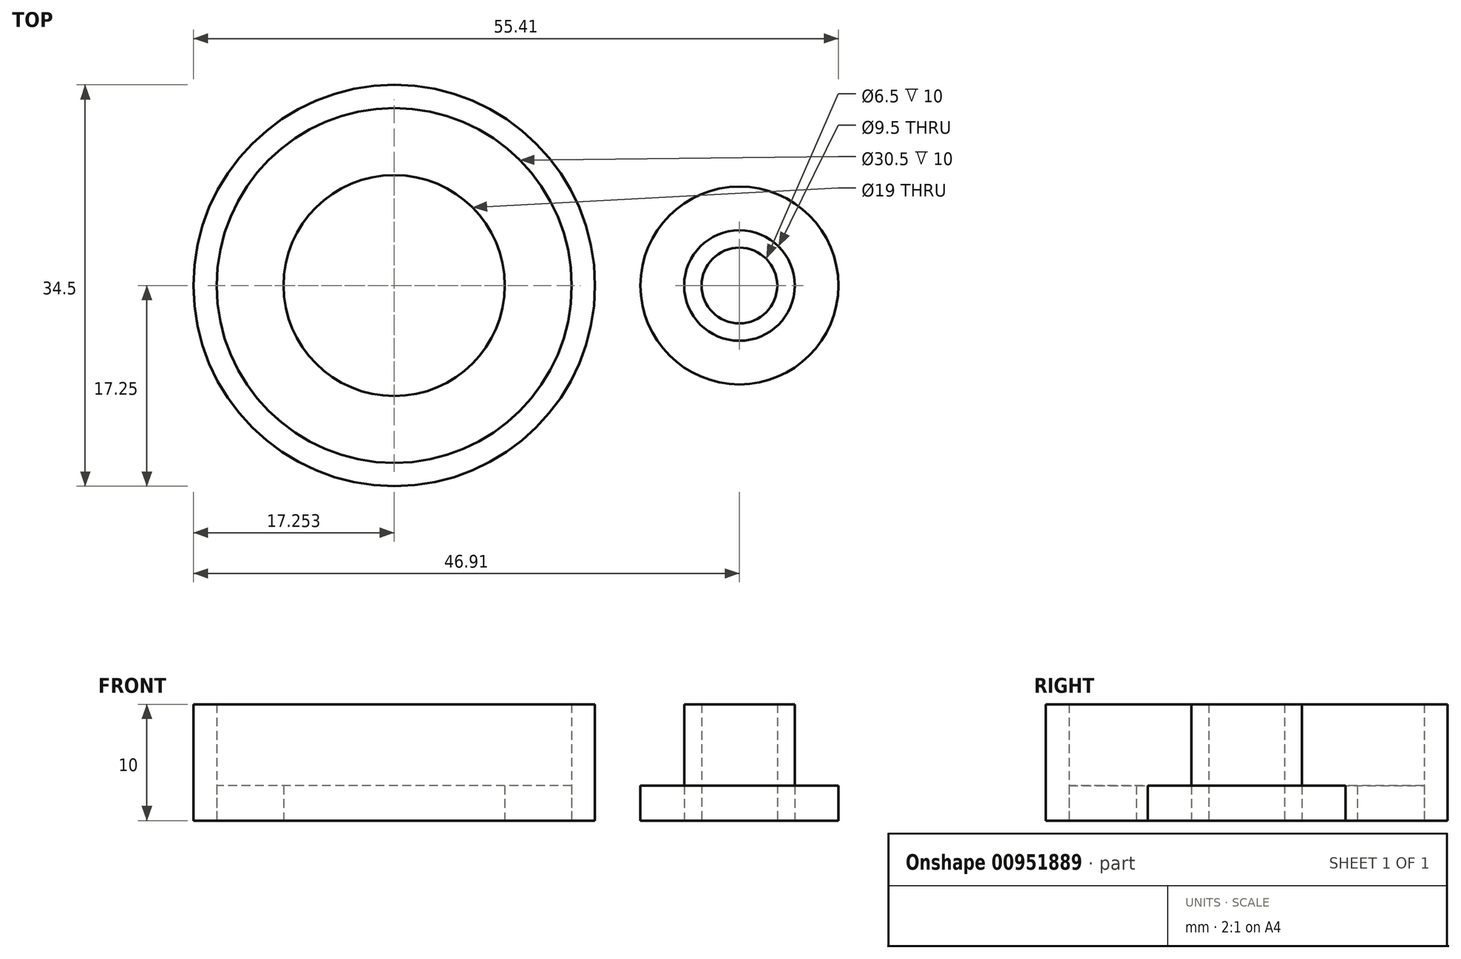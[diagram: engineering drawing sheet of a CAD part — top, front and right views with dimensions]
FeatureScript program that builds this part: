
annotation { "Feature Type Name" : "Feature", "Feature Type Description" : "" }
export const myFeature = defineFeature(function(context is Context, id is Id, definition is map)
    precondition{}
    {
        {
            var Q0;
            Q0=qCreatedBy(makeId("Top.planeOp"),FACE);
            var sketch = newSketch(context, id + "F0", { "sketchPlane" : qUnion([Q0])});
            skCircle(sketch, "E0", {"center": v(-39.15, 0) * mm, "radius": 15.25 * mm});
            skCircle(sketch, "E1", {"center": v(-39.15, 0) * mm, "radius": 17.25 * mm});
            skCircle(sketch, "E2", {"center": v(-9.5, 0) * mm, "radius": 4.75 * mm});
            skCircle(sketch, "E3", {"center": v(-9.5, 0) * mm, "radius": 8.5 * mm});
            skCircle(sketch, "E4", {"center": v(-9.5, 0) * mm, "radius": 3.25 * mm});
            skCircle(sketch, "E5", {"center": v(-39.15, 0) * mm, "radius": 9.5 * mm});
            skSolve(sketch);
        }
        {
            var Q0;
            Q0=makeQuery(id+"F0.imprint","IMPRINT",FACE,{"disambiguationData":[TD([[makeQuery(id+"F0.imprint","IMPRINT",EDGE,{"derivedFrom":sQuery(id+"F0.wireOp",EDGE,"E0")}),1.0]])]});
            var Q1;
            Q1=makeQuery(id+"F0.imprint","IMPRINT",FACE,{"disambiguationData":[TD([[makeQuery(id+"F0.imprint","IMPRINT",EDGE,{"derivedFrom":sQuery(id+"F0.wireOp",EDGE,"E2")}),-1.0]])]});
            extrude(context, id + "F1", {"entities" : qUnion([Q0, Q1]), "depth" : 3 * mm, "offsetDistance" : 25 * mm});
        }
        {
            var Q0;
            Q0=makeQuery(id+"F0.imprint","IMPRINT",FACE,{"disambiguationData":[TD([[makeQuery(id+"F0.imprint","IMPRINT",EDGE,{"derivedFrom":sQuery(id+"F0.wireOp",EDGE,"E0")}),-1.0]])]});
            var Q1;
            Q1=makeQuery(id+"F0.imprint","IMPRINT",FACE,{"disambiguationData":[TD([[makeQuery(id+"F0.imprint","IMPRINT",EDGE,{"derivedFrom":sQuery(id+"F0.wireOp",EDGE,"E2")}),1.0]])]});
            extrude(context, id + "F2", {"entities" : qUnion([Q0, Q1]), "depth" : 10 * mm, "offsetDistance" : 25 * mm});
        }
    });
